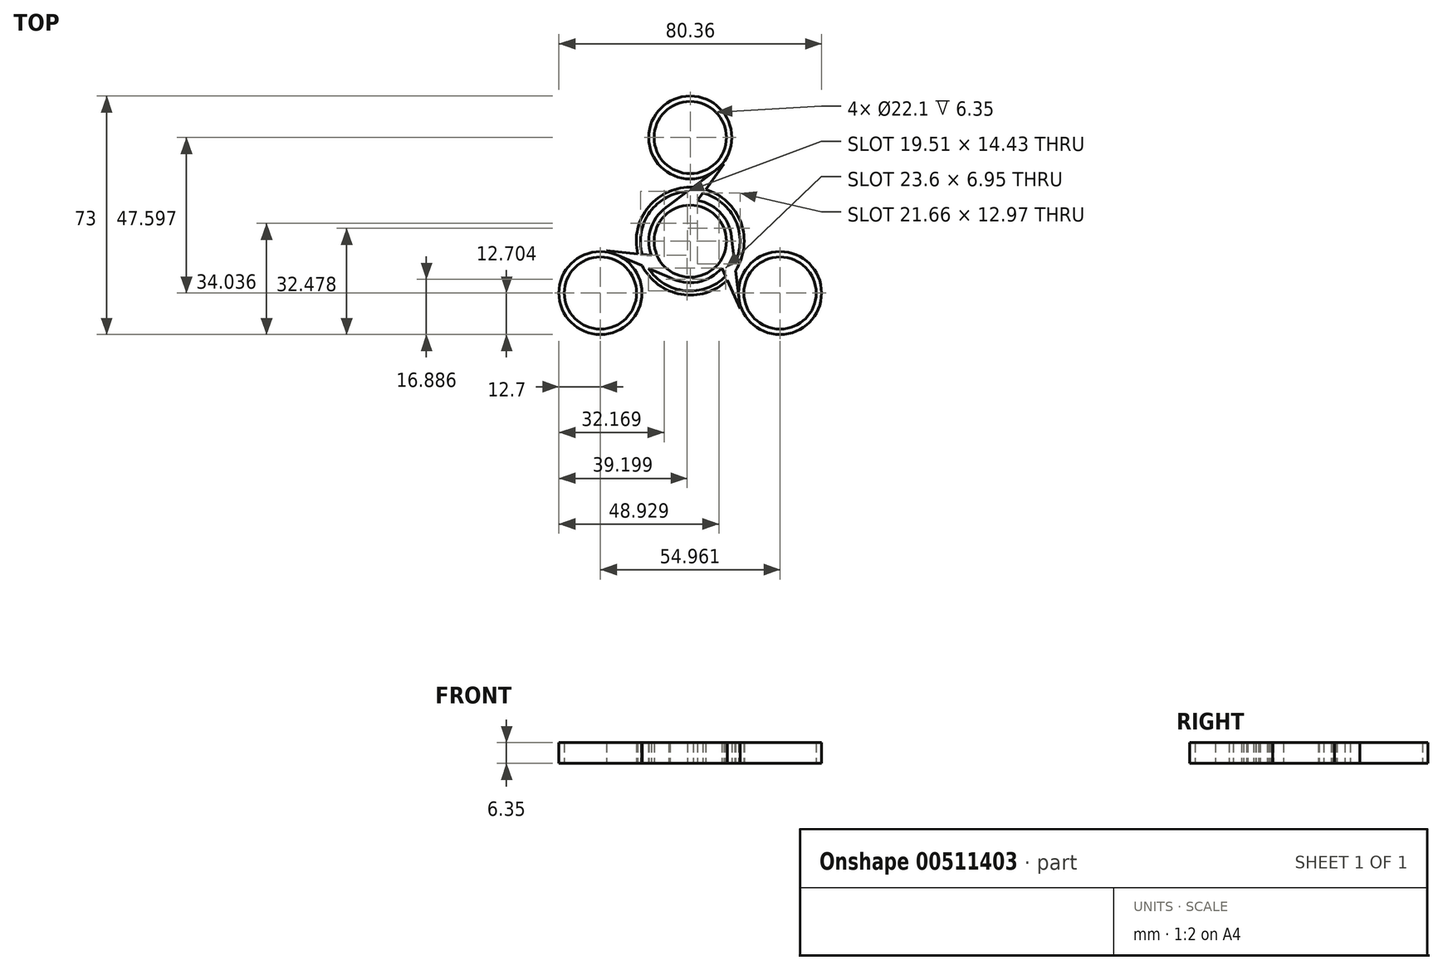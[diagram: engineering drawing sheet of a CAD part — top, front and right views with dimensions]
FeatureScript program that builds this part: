
annotation { "Feature Type Name" : "Feature", "Feature Type Description" : "" }
export const myFeature = defineFeature(function(context is Context, id is Id, definition is map)
    precondition{}
    {
        {
            var Q0;
            Q0=qCreatedBy(makeId("Top.planeOp"),FACE);
            var sketch = newSketch(context, id + "F0", { "sketchPlane" : qUnion([Q0])});
            skCircle(sketch, "E0", {"center": v(0, 0) * mm, "radius": 11.05 * mm});
            skCircle(sketch, "E1", {"center": v(0, 0) * mm, "radius": 12.7 * mm});
            skCircle(sketch, "E2", {"center": v(0, 0) * mm, "radius": 44.45 * mm});
            skCircle(sketch, "E3", {"center": v(0, 31.73) * mm, "radius": 11.05 * mm});
            skCircle(sketch, "E4", {"center": v(0, 31.73) * mm, "radius": 12.7 * mm});
            skLineSegment(sketch, "E5", {"start": v(-6.52, 10.9) * mm, "end": v(10.3, 23.59) * mm});
            skLineSegment(sketch, "E6", {"start": v(10.3, 23.59) * mm, "end": v(2.26, 12.5) * mm});
            skCircle(sketch, "E7.1.0", {"center": v(-27.48, -15.87) * mm, "radius": 11.05 * mm});
            skCircle(sketch, "E7.1.1", {"center": v(-27.48, -15.87) * mm, "radius": 12.7 * mm});
            skLineSegment(sketch, "E7.1.2", {"start": v(-6.18, -11.1) * mm, "end": v(-25.57, -2.88) * mm});
            skLineSegment(sketch, "E7.1.3", {"start": v(-25.57, -2.88) * mm, "end": v(-11.95, -4.29) * mm});
            skCircle(sketch, "E7.2.0", {"center": v(27.48, -15.87) * mm, "radius": 11.05 * mm});
            skCircle(sketch, "E7.2.1", {"center": v(27.48, -15.87) * mm, "radius": 12.7 * mm});
            skLineSegment(sketch, "E7.2.2", {"start": v(12.7, 0.2) * mm, "end": v(15.28, -20.7) * mm});
            skLineSegment(sketch, "E7.2.3", {"start": v(15.28, -20.7) * mm, "end": v(9.7, -8.2) * mm});
            skSolve(sketch);
        }
        {
            var Q0;
            {var subQ3=sQuery(id+"F0.wireOp",EDGE,"E6");Q0=makeQuery(id+"F0.imprint","IMPRINT",FACE,{"disambiguationData":[TD([[makeQuery(id+"F0.imprint","IMPRINT",EDGE,{"derivedFrom":subQ3}),-1.0]])]});}
            var Q1;
            Q1=makeQuery(id+"F0.imprint","IMPRINT",FACE,{"disambiguationData":[TD([[makeQuery(id+"F0.imprint","IMPRINT",EDGE,{"derivedFrom":sQuery(id+"F0.wireOp",EDGE,"E3")}),-1.0]])]});
            var Q2;
            Q2=makeQuery(id+"F0.imprint","IMPRINT",FACE,{"disambiguationData":[TD([[makeQuery(id+"F0.imprint","IMPRINT",EDGE,{"derivedFrom":sQuery(id+"F0.wireOp",EDGE,"E0")}),-1.0]])]});
            var Q3;
            {var subQ3=sQuery(id+"F0.wireOp",EDGE,"E7.1.3");Q3=makeQuery(id+"F0.imprint","IMPRINT",FACE,{"disambiguationData":[TD([[makeQuery(id+"F0.imprint","IMPRINT",EDGE,{"derivedFrom":subQ3}),-1.0]])]});}
            var Q4;
            Q4=makeQuery(id+"F0.imprint","IMPRINT",FACE,{"disambiguationData":[TD([[makeQuery(id+"F0.imprint","IMPRINT",EDGE,{"derivedFrom":sQuery(id+"F0.wireOp",EDGE,"E7.1.0")}),-1.0]])]});
            var Q5;
            Q5=makeQuery(id+"F0.imprint","IMPRINT",FACE,{"disambiguationData":[TD([[makeQuery(id+"F0.imprint","IMPRINT",EDGE,{"derivedFrom":sQuery(id+"F0.wireOp",EDGE,"E7.2.0")}),-1.0]])]});
            var Q6;
            {var subQ3=sQuery(id+"F0.wireOp",EDGE,"E7.2.3");Q6=makeQuery(id+"F0.imprint","IMPRINT",FACE,{"disambiguationData":[TD([[makeQuery(id+"F0.imprint","IMPRINT",EDGE,{"derivedFrom":subQ3}),-1.0]])]});}
            extrude(context, id + "F1", {"entities" : qUnion([Q0, Q1, Q2, Q3, Q4, Q5, Q6]), "depth" : 6.35 * mm});
        }
        {
            var Q0;
            Q0=qCreatedBy(makeId("Top.planeOp"),FACE);
            var sketch = newSketch(context, id + "F2", { "sketchPlane" : qUnion([Q0])});
            skCircle(sketch, "E8", {"center": v(0, 0) * mm, "radius": 15.24 * mm});
            skCircle(sketch, "E9", {"center": v(0, 0) * mm, "radius": 16.51 * mm});
            skSolve(sketch);
        }
        {
            var Q0;
            Q0=makeQuery(id+"F2.imprint","IMPRINT",FACE,{"disambiguationData":[TD([[makeQuery(id+"F2.imprint","IMPRINT",EDGE,{"derivedFrom":sQuery(id+"F2.wireOp",EDGE,"E8")}),-1.0]])]});
            extrude(context, id + "F3", {"entities" : qUnion([Q0]), "operationType" : NewBodyOperationType.ADD, "depth" : 6.35 * mm});
        }
    });
